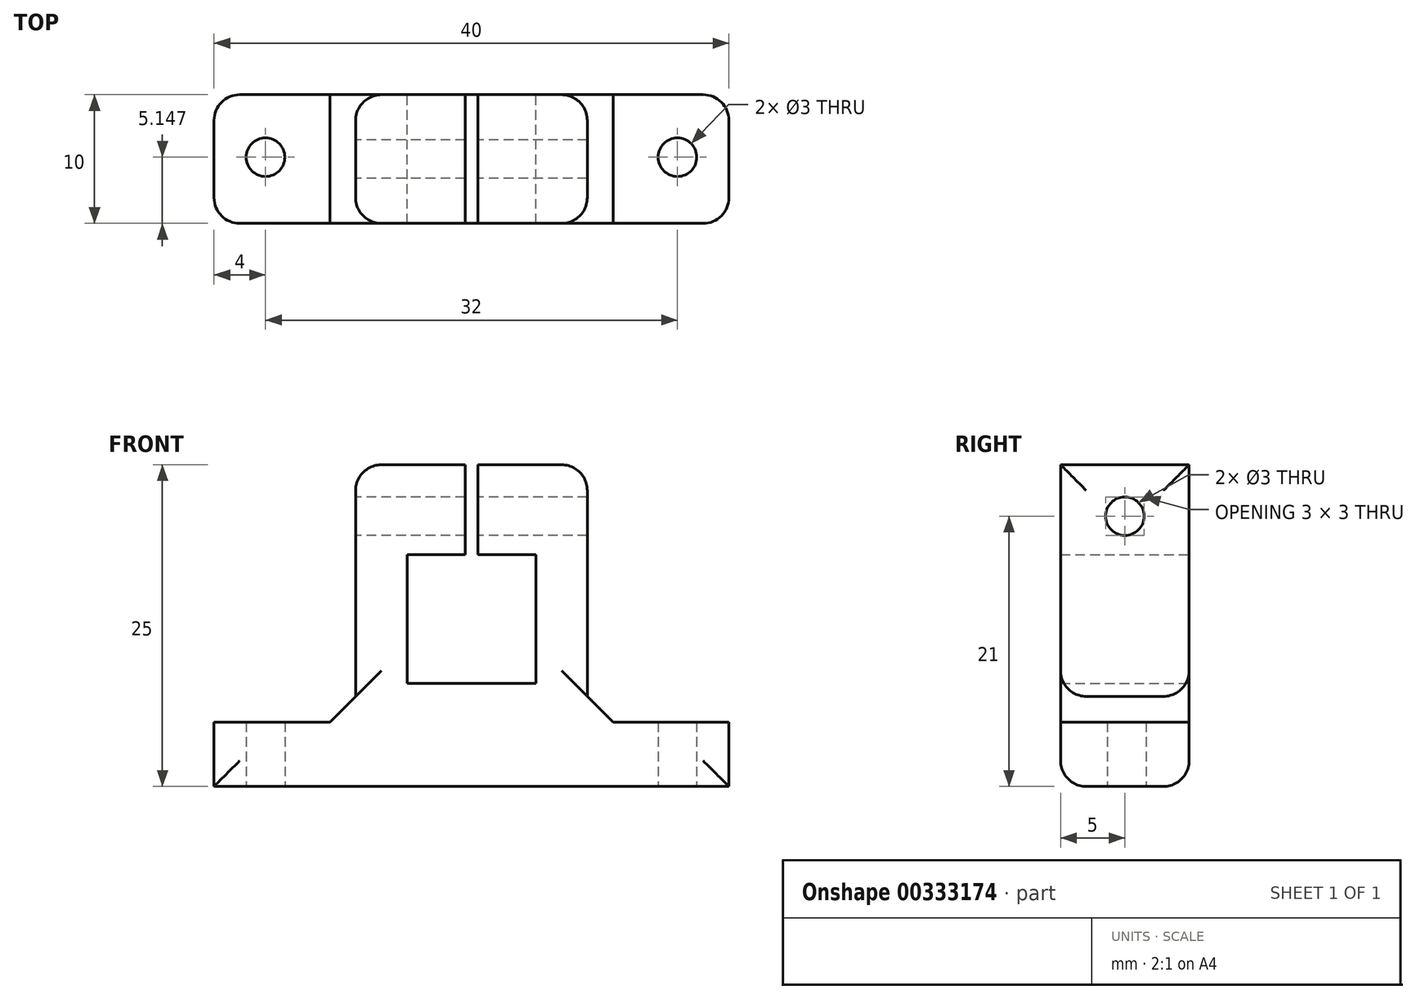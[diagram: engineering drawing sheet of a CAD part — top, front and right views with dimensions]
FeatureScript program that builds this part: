
annotation { "Feature Type Name" : "Feature", "Feature Type Description" : "" }
export const myFeature = defineFeature(function(context is Context, id is Id, definition is map)
    precondition{}
    {
        {
            var Q0;
            Q0=qCreatedBy(makeId("Front.planeOp"),FACE);
            var sketch = newSketch(context, id + "F0", { "sketchPlane" : qUnion([Q0])});
            skLineSegment(sketch, "E0.bottom", {"start": v(20, -11.5) * mm, "end": v(-20, -11.5) * mm});
            skLineSegment(sketch, "E0.top", {"start": v(9, 11.5) * mm, "end": v(-9, 11.5) * mm});
            skLineSegment(sketch, "E0.left", {"start": v(20, -11.5) * mm, "end": v(20, -6.5) * mm});
            skLineSegment(sketch, "E0.right", {"start": v(-20, -11.5) * mm, "end": v(-20, -6.5) * mm});
            skPoint(sketch, "E0.middle", {"position": v(0, 0) * mm});
            skLineSegment(sketch, "E1", {"start": v(-20, -6.5) * mm, "end": v(-9, -6.5) * mm});
            skLineSegment(sketch, "E2", {"start": v(-9, -6.5) * mm, "end": v(-9, 11.5) * mm});
            skLineSegment(sketch, "E3.MirrorCS", {"start": v(9, -6.5) * mm, "end": v(9, 11.5) * mm});
            skPoint(sketch, "E4.orphan", {"position": v(-20, 11.5) * mm});
            skLineSegment(sketch, "E5.trimOffspring", {"start": v(9, -6.5) * mm, "end": v(20, -6.5) * mm});
            skPoint(sketch, "E6.orphan", {"position": v(20, 11.5) * mm});
            skPoint(sketch, "E7.start.orphan", {"position": v(-0.5, 11.5) * mm});
            skPoint(sketch, "E8.orphan", {"position": v(-1.34, 4.87) * mm});
            skPoint(sketch, "E9.MirrorCS.start.orphan", {"position": v(0.5, 11.5) * mm});
            skPoint(sketch, "E10.start.orphan", {"position": v(1.34, 4.87) * mm});
            skLineSegment(sketch, "E11.bottom", {"start": v(5, -3.5) * mm, "end": v(-5, -3.5) * mm});
            skLineSegment(sketch, "E11.top", {"start": v(5, 6.5) * mm, "end": v(-5, 6.5) * mm});
            skLineSegment(sketch, "E11.left", {"start": v(5, -3.5) * mm, "end": v(5, 6.5) * mm});
            skLineSegment(sketch, "E11.right", {"start": v(-5, -3.5) * mm, "end": v(-5, 6.5) * mm});
            skPoint(sketch, "E11.middle", {"position": v(0, 1.5) * mm});
            skLineSegment(sketch, "E12", {"start": v(-0.5, 11.5) * mm, "end": v(-0.5, 6.5) * mm});
            skLineSegment(sketch, "E13.MirrorCS", {"start": v(0.5, 11.5) * mm, "end": v(0.5, 6.5) * mm});
            skSolve(sketch);
        }
        {
            var Q0;
            Q0=makeQuery(id+"F0.imprint","IMPRINT",FACE,{"disambiguationData":[TD([[makeQuery(id+"F0.imprint","IMPRINT",EDGE,{"derivedFrom":sQuery(id+"F0.wireOp",EDGE,"E0.bottom")}),-1.0]])]});
            extrude(context, id + "F1", {"entities" : qUnion([Q0]), "depth" : 10 * mm});
        }
        {
            var Q0;
            Q0=makeQuery(id+"F1.opExtrude","SWEPT_FACE",FACE,{"disambiguationData":[OSD([sQuery(id+"F0.wireOp",EDGE,"E0.bottom")])]});
            var sketch = newSketch(context, id + "F2", { "sketchPlane" : qUnion([Q0])});
            skCircle(sketch, "E14", {"center": v(16, 4.85) * mm, "radius": 1.5 * mm});
            skCircle(sketch, "E15.MirrorC", {"center": v(-16, 4.85) * mm, "radius": 1.5 * mm});
            skSolve(sketch);
        }
        {
            var Q0;
            Q0=qSketchRegion(id+"F2",true);
            extrude(context, id + "F3", {"entities" : qUnion([Q0]), "operationType" : NewBodyOperationType.REMOVE, "oppositeDirection" : true, "depth" : 10.5 * mm});
        }
        {
            var Q0;
            Q0=makeQuery(id+"F1.opExtrude","SWEPT_FACE",FACE,{"disambiguationData":[OSD([sQuery(id+"F0.wireOp",EDGE,"E2")])]});
            var sketch = newSketch(context, id + "F4", { "sketchPlane" : qUnion([Q0])});
            skCircle(sketch, "E16", {"center": v(5, 9.5) * mm, "radius": 1.5 * mm});
            skSolve(sketch);
        }
        {
            var Q0;
            Q0=qSketchRegion(id+"F4",true);
            extrude(context, id + "F5", {"entities" : qUnion([Q0]), "operationType" : NewBodyOperationType.REMOVE, "oppositeDirection" : true, "depth" : 25 * mm});
        }
        {
            var Q0;
            {var subQ0=sQuery(id+"F0.wireOp",EDGE,"E0.top");Q0=makeQuery(id+"F1.opExtrude","SWEPT_FACE",FACE,{"disambiguationData":[OSD([subQ0]),TDD([makeQuery(id+"F0.imprint","IMPRINT",EDGE,{"disambiguationData":[TD([[makeQuery(id+"F0.imprint","INTERSECT",VERTEX,{"derivedFrom":[subQ0,sQuery(id+"F0.wireOp",EDGE,"E3.MirrorCS")]}),-1.0]])],"derivedFrom":subQ0})])]});}
            var Q1;
            {var subQ0=sQuery(id+"F0.wireOp",EDGE,"E0.top");Q1=makeQuery(id+"F1.opExtrude","SWEPT_FACE",FACE,{"disambiguationData":[OSD([subQ0]),TDD([makeQuery(id+"F0.imprint","IMPRINT",EDGE,{"disambiguationData":[TD([[makeQuery(id+"F0.imprint","INTERSECT",VERTEX,{"derivedFrom":[subQ0,sQuery(id+"F0.wireOp",EDGE,"E2")]}),1.0]])],"derivedFrom":subQ0})])]});}
            extrude(context, id + "F6", {"entities" : qUnion([Q0, Q1]), "operationType" : NewBodyOperationType.ADD, "depth" : 2 * mm});
        }
        {
            var Q0;
            Q0=makeQuery(id+"F1.opExtrude","SWEPT_EDGE",EDGE,{"disambiguationData":[OSD([sQuery(id+"F0.wireOp",EDGE,"E1"),sQuery(id+"F0.wireOp",EDGE,"E2")])]});
            chamfer(context, id + "F7", {"entities" : qUnion([Q0]), "width" : 2 * mm, "tangentPropagation" : true});
        }
        {
            var Q0;
            Q0=makeQuery(id+"F1.opExtrude","SWEPT_EDGE",EDGE,{"disambiguationData":[OSD([sQuery(id+"F0.wireOp",EDGE,"E3.MirrorCS"),sQuery(id+"F0.wireOp",EDGE,"E5.trimOffspring")])]});
            chamfer(context, id + "F8", {"entities" : qUnion([Q0]), "width" : 2 * mm, "tangentPropagation" : true});
        }
        {
            var Q0;
            Q0=makeQuery(id+"F1.opExtrude","CAP_EDGE",EDGE,{"disambiguationData":[OSD([sQuery(id+"F0.wireOp",EDGE,"E0.right")])],"isStart":false});
            var Q1;
            Q1=makeQuery(id+"F1.opExtrude","CAP_EDGE",EDGE,{"disambiguationData":[OSD([sQuery(id+"F0.wireOp",EDGE,"E0.right")])],"isStart":true});
            var Q2;
            Q2=makeQuery(id+"F1.opExtrude","CAP_EDGE",EDGE,{"disambiguationData":[OSD([sQuery(id+"F0.wireOp",EDGE,"E0.left")])],"isStart":true});
            var Q3;
            Q3=makeQuery(id+"F1.opExtrude","CAP_EDGE",EDGE,{"disambiguationData":[OSD([sQuery(id+"F0.wireOp",EDGE,"E0.left")])],"isStart":false});
            var Q4;
            Q4=makeQuery(id+"F6.opExtrude","CAP_EDGE",EDGE,{"disambiguationData":[OSD([sQuery(id+"F0.wireOp",EDGE,"E0.top"),sQuery(id+"F0.wireOp",EDGE,"E3.MirrorCS")])],"isStart":false});
            var Q5;
            Q5=makeQuery(id+"F6.opExtrude","CAP_EDGE",EDGE,{"disambiguationData":[OSD([sQuery(id+"F0.wireOp",EDGE,"E0.top"),sQuery(id+"F0.wireOp",EDGE,"E2")])],"isStart":false});
            var Q6;
            {var subQ0=sQuery(id+"F0.wireOp",EDGE,"E2");var subQ1=sQuery(id+"F0.wireOp",EDGE,"E0.top");Q6=makeQuery(id+"F6.boolean.opBoolean","MERGE",EDGE,{"derivedFrom":[makeQuery(id+"F1.opExtrude","CAP_EDGE",EDGE,{"disambiguationData":[OSD([subQ0])],"isStart":false}),makeQuery(id+"F6.opExtrude","SWEPT_EDGE",EDGE,{"disambiguationData":[OSD([subQ1,subQ0]),TDD([makeQuery(id+"F1.opExtrude","CAP_VERTEX",VERTEX,{"disambiguationData":[OSD([subQ1,subQ0])],"isStart":false})])]})]});}
            var Q7;
            {var subQ0=sQuery(id+"F0.wireOp",EDGE,"E3.MirrorCS");var subQ1=sQuery(id+"F0.wireOp",EDGE,"E0.top");Q7=makeQuery(id+"F6.boolean.opBoolean","MERGE",EDGE,{"derivedFrom":[makeQuery(id+"F1.opExtrude","CAP_EDGE",EDGE,{"disambiguationData":[OSD([subQ0])],"isStart":false}),makeQuery(id+"F6.opExtrude","SWEPT_EDGE",EDGE,{"disambiguationData":[OSD([subQ1,subQ0]),TDD([makeQuery(id+"F1.opExtrude","CAP_VERTEX",VERTEX,{"disambiguationData":[OSD([subQ1,subQ0])],"isStart":false})])]})]});}
            var Q8;
            {var subQ0=sQuery(id+"F0.wireOp",EDGE,"E3.MirrorCS");var subQ1=sQuery(id+"F0.wireOp",EDGE,"E0.top");Q8=makeQuery(id+"F6.boolean.opBoolean","MERGE",EDGE,{"derivedFrom":[makeQuery(id+"F1.opExtrude","CAP_EDGE",EDGE,{"disambiguationData":[OSD([subQ0])],"isStart":true}),makeQuery(id+"F6.opExtrude","SWEPT_EDGE",EDGE,{"disambiguationData":[OSD([subQ1,subQ0]),TDD([makeQuery(id+"F1.opExtrude","CAP_VERTEX",VERTEX,{"disambiguationData":[OSD([subQ1,subQ0])],"isStart":true})])]})]});}
            var Q9;
            {var subQ0=sQuery(id+"F0.wireOp",EDGE,"E2");var subQ1=sQuery(id+"F0.wireOp",EDGE,"E0.top");Q9=makeQuery(id+"F6.boolean.opBoolean","MERGE",EDGE,{"derivedFrom":[makeQuery(id+"F1.opExtrude","CAP_EDGE",EDGE,{"disambiguationData":[OSD([subQ0])],"isStart":true}),makeQuery(id+"F6.opExtrude","SWEPT_EDGE",EDGE,{"disambiguationData":[OSD([subQ1,subQ0]),TDD([makeQuery(id+"F1.opExtrude","CAP_VERTEX",VERTEX,{"disambiguationData":[OSD([subQ1,subQ0])],"isStart":true})])]})]});}
            var Q10;
            Q10=makeQuery(id+"F1.opExtrude","CAP_EDGE",EDGE,{"disambiguationData":[OSD([sQuery(id+"F0.wireOp",EDGE,"E0.bottom")])],"isStart":true});
            var Q11;
            Q11=makeQuery(id+"F1.opExtrude","CAP_EDGE",EDGE,{"disambiguationData":[OSD([sQuery(id+"F0.wireOp",EDGE,"E0.bottom")])],"isStart":false});
            fillet(context, id + "F9", {"entities" : qUnion([Q0, Q1, Q2, Q3, Q4, Q5, Q6, Q7, Q8, Q9, Q10, Q11]), "radius" : 2 * mm, "tangentPropagation" : true, "allowEdgeOverflow" : false});
        }
    });
